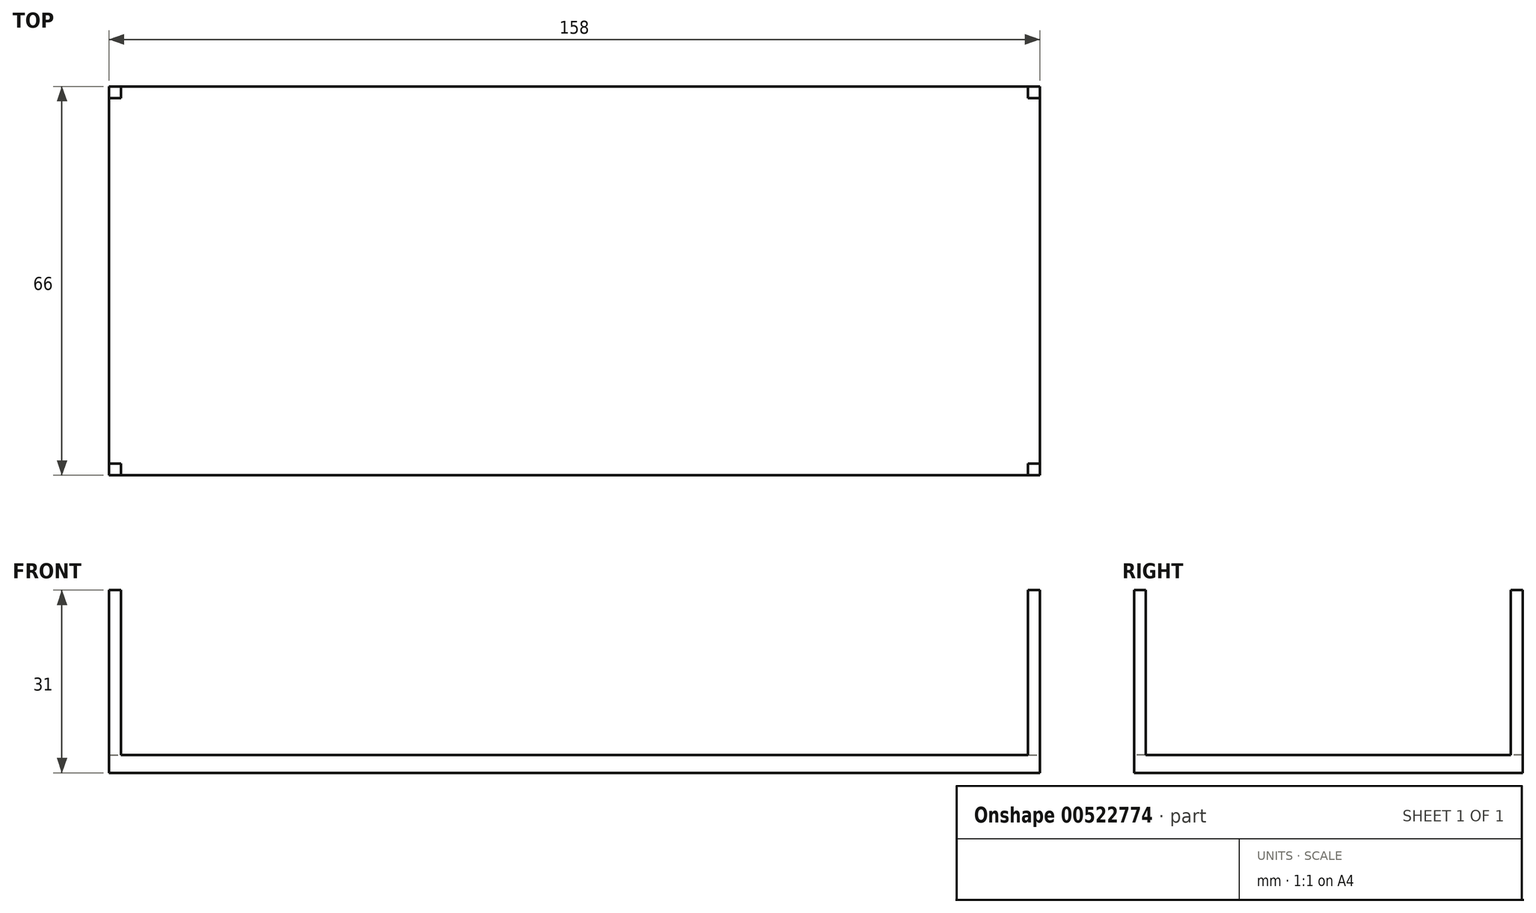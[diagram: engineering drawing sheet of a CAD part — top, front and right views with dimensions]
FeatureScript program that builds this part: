
annotation { "Feature Type Name" : "Feature", "Feature Type Description" : "" }
export const myFeature = defineFeature(function(context is Context, id is Id, definition is map)
    precondition{}
    {
        {
            var Q0;
            Q0=qCreatedBy(makeId("Top.planeOp"),FACE);
            var sketch = newSketch(context, id + "F0", { "sketchPlane" : qUnion([Q0])});
            skLineSegment(sketch, "E0", {"start": v(-43.73, 10.26) * mm, "end": v(114.27, 10.26) * mm});
            skLineSegment(sketch, "E1", {"start": v(114.27, 10.26) * mm, "end": v(114.27, -55.74) * mm});
            skLineSegment(sketch, "E2", {"start": v(114.27, -55.74) * mm, "end": v(-43.73, -55.74) * mm});
            skLineSegment(sketch, "E3", {"start": v(-43.73, -55.74) * mm, "end": v(-43.73, 10.26) * mm});
            skSolve(sketch);
        }
        {
            var Q0;
            Q0=makeQuery(id+"F0.imprint","IMPRINT",FACE,{"disambiguationData":[TD([[makeQuery(id+"F0.imprint","IMPRINT",EDGE,{"derivedFrom":sQuery(id+"F0.wireOp",EDGE,"E0")}),-1.0]])]});
            extrude(context, id + "F1", {"entities" : qUnion([Q0]), "depth" : 3 * mm, "offsetDistance" : 25 * mm});
        }
        {
            var Q0;
            Q0=makeQuery(id+"F1.opExtrude","CAP_FACE",FACE,{"disambiguationData":[OSD([sQuery(id+"F0.wireOp",EDGE,"E0"),sQuery(id+"F0.wireOp",EDGE,"E1"),sQuery(id+"F0.wireOp",EDGE,"E2"),sQuery(id+"F0.wireOp",EDGE,"E3")])],"isStart":false});
            var sketch = newSketch(context, id + "F2", { "sketchPlane" : qUnion([Q0])});
            skLineSegment(sketch, "E4.bottom", {"start": v(-43.73, 10.26) * mm, "end": v(114.27, 10.26) * mm});
            skLineSegment(sketch, "E4.top", {"start": v(-43.73, -55.74) * mm, "end": v(114.27, -55.74) * mm});
            skLineSegment(sketch, "E4.left", {"start": v(-43.73, 10.26) * mm, "end": v(-43.73, -55.74) * mm});
            skLineSegment(sketch, "E4.right", {"start": v(114.27, 10.26) * mm, "end": v(114.27, -55.74) * mm});
            skLineSegment(sketch, "E5.0", {"start": v(-43.73, 8.26) * mm, "end": v(114.27, 8.26) * mm});
            skLineSegment(sketch, "E6.0", {"start": v(-43.73, -53.74) * mm, "end": v(114.27, -53.74) * mm});
            skLineSegment(sketch, "E7.0", {"start": v(-41.73, 10.26) * mm, "end": v(-41.73, -55.74) * mm});
            skLineSegment(sketch, "E8.0", {"start": v(112.27, 10.26) * mm, "end": v(112.27, -55.74) * mm});
            skLineSegment(sketch, "E9.bottom", {"start": v(-41.73, -53.74) * mm, "end": v(112.27, -53.74) * mm});
            skLineSegment(sketch, "E9.top", {"start": v(-41.73, 8.26) * mm, "end": v(112.27, 8.26) * mm});
            skLineSegment(sketch, "E9.left", {"start": v(-41.73, -53.74) * mm, "end": v(-41.73, 8.26) * mm});
            skLineSegment(sketch, "E9.right", {"start": v(112.27, -53.74) * mm, "end": v(112.27, 8.26) * mm});
            skSolve(sketch);
        }
        {
            var Q0;
            {var subQ5=sQuery(id+"F2.wireOp",EDGE,"E9.bottom");Q0=makeQuery(id+"F2.imprint","IMPRINT",FACE,{"disambiguationData":[TD([[makeQuery(id+"F2.imprint","IMPRINT",EDGE,{"derivedFrom":subQ5}),-1.0]])]});}
            var Q1;
            {var subQ0=sQuery(id+"F2.wireOp",EDGE,"E4.left");var subQ1=sQuery(id+"F2.wireOp",EDGE,"E4.top");var subQ2=makeQuery(id+"F2.imprint","INTERSECT",VERTEX,{"derivedFrom":[subQ1,subQ0]});Q1=makeQuery(id+"F2.imprint","IMPRINT",FACE,{"disambiguationData":[TD([[makeQuery(id+"F2.imprint","IMPRINT",EDGE,{"disambiguationData":[TD([[subQ2,1.0]])],"derivedFrom":subQ1}),-1.0]])]});}
            var Q2;
            {var subQ5=sQuery(id+"F2.wireOp",EDGE,"E9.left");Q2=makeQuery(id+"F2.imprint","IMPRINT",FACE,{"disambiguationData":[TD([[makeQuery(id+"F2.imprint","IMPRINT",EDGE,{"derivedFrom":subQ5}),1.0]])]});}
            var Q3;
            {var subQ0=sQuery(id+"F2.wireOp",EDGE,"E4.left");var subQ1=sQuery(id+"F2.wireOp",EDGE,"E4.bottom");var subQ2=makeQuery(id+"F2.imprint","INTERSECT",VERTEX,{"derivedFrom":[subQ1,subQ0]});Q3=makeQuery(id+"F2.imprint","IMPRINT",FACE,{"disambiguationData":[TD([[makeQuery(id+"F2.imprint","IMPRINT",EDGE,{"disambiguationData":[TD([[subQ2,-1.0]])],"derivedFrom":subQ1}),-1.0]])]});}
            var Q4;
            {var subQ5=sQuery(id+"F2.wireOp",EDGE,"E9.top");Q4=makeQuery(id+"F2.imprint","IMPRINT",FACE,{"disambiguationData":[TD([[makeQuery(id+"F2.imprint","IMPRINT",EDGE,{"derivedFrom":subQ5}),1.0]])]});}
            var Q5;
            {var subQ0=sQuery(id+"F2.wireOp",EDGE,"E4.right");var subQ1=sQuery(id+"F2.wireOp",EDGE,"E4.bottom");var subQ2=makeQuery(id+"F2.imprint","INTERSECT",VERTEX,{"derivedFrom":[subQ1,subQ0]});Q5=makeQuery(id+"F2.imprint","IMPRINT",FACE,{"disambiguationData":[TD([[makeQuery(id+"F2.imprint","IMPRINT",EDGE,{"disambiguationData":[TD([[subQ2,1.0]])],"derivedFrom":subQ1}),-1.0]])]});}
            var Q6;
            {var subQ5=sQuery(id+"F2.wireOp",EDGE,"E9.right");Q6=makeQuery(id+"F2.imprint","IMPRINT",FACE,{"disambiguationData":[TD([[makeQuery(id+"F2.imprint","IMPRINT",EDGE,{"derivedFrom":subQ5}),-1.0]])]});}
            var Q7;
            {var subQ0=sQuery(id+"F2.wireOp",EDGE,"E4.right");var subQ1=sQuery(id+"F2.wireOp",EDGE,"E4.top");var subQ2=makeQuery(id+"F2.imprint","INTERSECT",VERTEX,{"derivedFrom":[subQ1,subQ0]});Q7=makeQuery(id+"F2.imprint","IMPRINT",FACE,{"disambiguationData":[TD([[makeQuery(id+"F2.imprint","IMPRINT",EDGE,{"disambiguationData":[TD([[subQ2,-1.0]])],"derivedFrom":subQ1}),-1.0]])]});}
            extrude(context, id + "F3", {"entities" : qUnion([Q0, Q1, Q2, Q3, Q4, Q5, Q6, Q7]), "operationType" : NewBodyOperationType.ADD, "depth" : 28 * mm, "offsetDistance" : 25 * mm});
        }
    });
